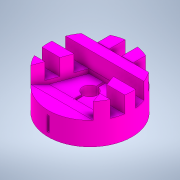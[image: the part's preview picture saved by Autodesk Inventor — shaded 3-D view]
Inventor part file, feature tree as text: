
AUTODESK INVENTOR PART (.ipt)
format: ipt  version: 2020 (Build 240168000, 168)  size: 284,672 bytes
history: native  units: mm
features: extrude x7, sketch x6, draft x2, plane x2, chamfer x1, projected_geometry x1
ambient origin geometry x8: Origin, YZ Plane, XZ Plane, XY Plane, X Axis, Y Axis, Z Axis, Center Point
bodies: Solid1 (feature_tree)
feature tree (19):
  sketch  "Sketch1"  dims[d0=15.0mm d1=10.0mm]
  extrude  "Extrusion1"  Depth=10.0mm
  extrude  "Extrusion2"  Depth=24.0mm TaperAngle=0.0deg
  sketch  "Sketch3"  dims[d5=30.0mm d6=0.0mm d7=7.0mm d8=0.0mm]
  extrude  "Extrusion3"  Depth=7.0mm TaperAngle=0.0deg
  extrude  "Extrusion4"  Depth=7.0mm
  draft  "FaceDraft1"
  draft  "FaceDraft2"
  extrude  "Extrusion5"  Depth=2.0mm TaperAngle=0.0deg
  chamfer  "Chamfer1"  Distance=3.490659mm
  plane  "Work Plane1"
  extrude  "Extrusion6"  Depth=1.0mm
  plane  "Work Plane2"
  extrude  "Extrusion7"  Depth=10.0mm
  sketch  "Sketch2"  dims[d2=40.0mm d3=24.0mm d4=0.0mm]
  projected_geometry  "Projected Loop1"
  sketch  "Sketch4"  dims[d9=11.0mm d10=7.0mm]
  sketch  "Sketch5"  dims[d13=2.0mm d14=0.0mm d15=2.0mm d16=0.0mm]
  sketch  "Sketch6"  dims[d17=3.490659mm d18=3.490659mm d19=1.0mm d20=50.0mm d21=7.0mm d22=2.0mm d23=0.0mm d24=6.4mm d25=2.0mm d26=45.0deg d27=0.2mm d28=0.2mm d29=0.2mm d30=0.2mm d31=0.2mm d32=0.2mm d33=0.2mm d34=4.9mm d35=4.9mm d36=4.9mm d37=4.9mm d38=4.9mm d39=0.0mm d40=0.0mm d41=0.2mm d42=0.2mm d43=0.2mm d44=0.2mm d45=0.2mm d46=0.2mm d47=5.5mm d48=5.5mm d49=5.5mm d50=10.0mm d51=0.0mm]
